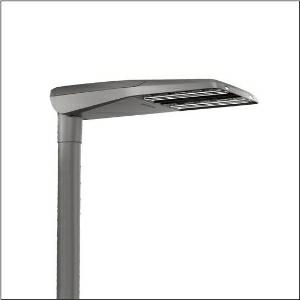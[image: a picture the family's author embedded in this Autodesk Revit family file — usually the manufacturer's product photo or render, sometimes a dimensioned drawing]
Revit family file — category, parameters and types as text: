
# Revit family: streetlight_sl_11_iq_midi___st1_2a_5xc3a51f08le_94b4
name_source: partatom
category: Lighting Fixtures
units: mm (PartAtom-declared; Revit-internal decimal feet)

## family parameters
Cut with Voids When Loaded = No
Host = Face
Light Source = No
Part Type = Normal
Room Calculation Point = No
Round Connector Dimension = Use Diameter
Shared = No

## types (1)
- --- (1 x LED, 9210 lm, 60.4 W, 3000K)
    Apparent Load = 60 VA
    CIE Flux Codes = 32 70 96 100 100
    Color Rendering = 70
    Color Temperature = 3000K
    Default Elevation = 1800 mm
    Description = Streetlight SL 11 iQ midi, mast luminaire, primary light control with 3 zone facetted reflector, of plastic, silver coated, highly specular, primary optical cover: cover, of PMMA, transparent, light distribution: ST1.2a, light emission: direct distribution, primary light characteristic: asymmetric, installation type: post-top, side-entry, LED, High Power LED, rated luminous flux: 9.210lm, luminous efficacy: 153lm/W, light colour: 730, colour temperature: 3000K, control: Street-Remote, optimised constant luminous flux control (CLO 2.0), Desk-Remote (wireless, voltage-free reading and setting of iQ features in the workshop via application-optimized NFC function/RFID function), Light-Fading, Smart-Wire, Night-Set, Lumen-Switch, Temp-Guard, Auto-Match, with cable H07RN-F 5x 1.5mm², mains connection: 220..240V, AC, 50/60Hz, connection cable pre-assembled, cable length: 8,5m, start of lifetime: 60W, end of lifetime: 63W, reduction: 30W, luminaire housing, of diecast aluminium, powder-coated, Siteco® metallic grey (DB 702S), length: 780mm, width: 376mm, height: 118mm, spigot size: 60/76mm (post-top) and 42/60/76mm (side-entry), mast flange for spigot size: 42mm: 5XC10008XM4, 60mm: 5XC10008XM2, 76/60mm: 5XC10108XM1, equipment: standard, protection rating (complete): IP66, insulation class (complete): insulation class II (safety insulation), certification: CE, ENEC, VDE, impact resistance: IK09, permissible operating ambient temperature for outdoor applications: -25..+50°C, standard-compliant lighting for roads and squares, packaging unit: 1 piece

Light Distribution: ST1.2a
    Height = 118 mm
    Lamp = 1 x LED
    Lamp Light Flux = 9210 lm
    Lamp Power = 60.4 W
    Lamp count = 1
    Length = 780 mm
    Luminous efficacy = 152 lm/W
    Manufacturer = Siteco
    ModVariant = No
    Model = 5XC3A51F08LE
    Number of Poles = 1
    OnlyDefault = Yes
    Power Factor = 1
    Product Name = Streetlight SL 11 iQ midi | ST1.2a
    Product group = mast luminaire | pylon top
    ProductGroupID = 6100
    Protection Class = Protection class II
    Protection Degree = IP 66
    RLX_Detail_Level = 1
    RlxData = <blob elided: 70349 chars, md5=06fd212a>
    Socket = socket
    Standby Power = 0 W
    System Light Flux = 9210 lm
    System Power = 60 W
    Type Comments = factory setting: luminous flux: 100 % | dim-lin: 254 | 520 mA
    Type Image = l_1005960.jpg
    URL = http://relux.com
    VarID = @adj_120733
    Voltage = 0 V
    Weight = 0.00 kg
    Width = 376 mm

## geometry (parser evidence)
native form markers: Blend x4, Sweep x9
no freeform markers — native parametric forms only
